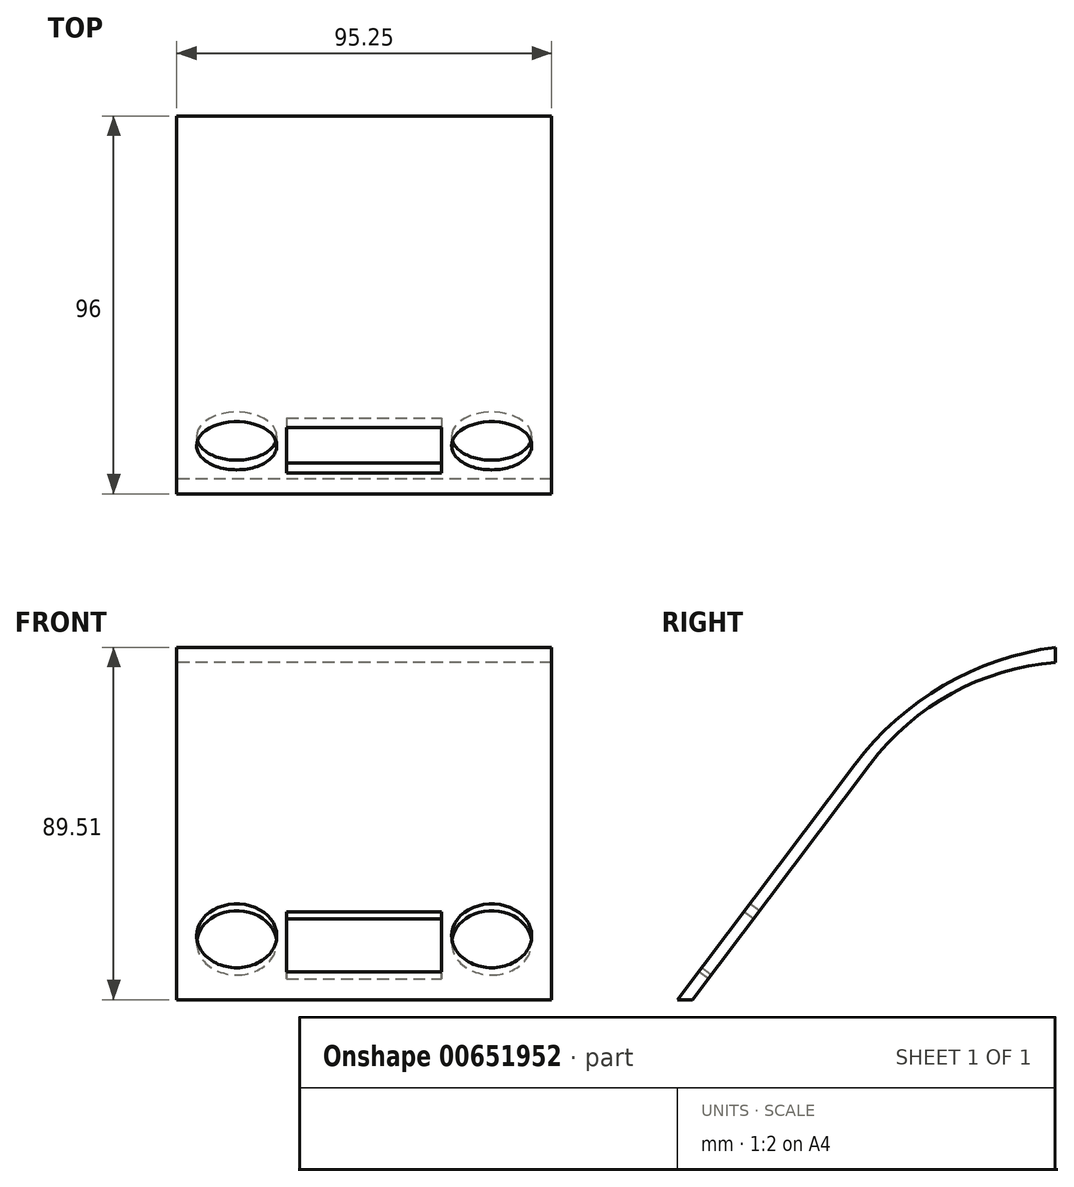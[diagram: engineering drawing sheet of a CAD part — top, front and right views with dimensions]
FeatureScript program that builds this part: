
annotation { "Feature Type Name" : "Feature", "Feature Type Description" : "" }
export const myFeature = defineFeature(function(context is Context, id is Id, definition is map)
    precondition{}
    {
        {
            var Q0;
            Q0=qCreatedBy(makeId("Right.planeOp"),FACE);
            var sketch = newSketch(context, id + "F0", { "sketchPlane" : qUnion([Q0])});
            skLineSegment(sketch, "E0", {"start": v(-8.65, 12.23) * mm, "end": v(-53.69, -47.57) * mm});
            skLineSegment(sketch, "E1", {"start": v(-53.69, -47.57) * mm, "end": v(-49.88, -47.57) * mm});
            skLineSegment(sketch, "E2", {"start": v(-49.88, -47.57) * mm, "end": v(-4.84, 12.23) * mm});
            skArc(sketch, "E3", {"start": v(42.31, 41.94) * mm, "mid": v(13.84, 32.22) * mm, "end": v(-8.65, 12.23) * mm});
            skArc(sketch, "E4", {"start": v(42.31, 38.13) * mm, "mid": v(15.96, 30.24) * mm, "end": v(-4.84, 12.23) * mm});
            skLineSegment(sketch, "E5", {"start": v(42.31, 41.94) * mm, "end": v(42.31, 38.13) * mm});
            skSolve(sketch);
        }
        {
            var Q0;
            Q0=makeQuery(id+"F0.imprint","IMPRINT",FACE,{"disambiguationData":[TD([[makeQuery(id+"F0.imprint","IMPRINT",EDGE,{"derivedFrom":sQuery(id+"F0.wireOp",EDGE,"E0")}),1.0]])]});
            extrude(context, id + "F1", {"entities" : qUnion([Q0]), "depth" : 95.25 * mm, "offsetDistance" : 25.4 * mm});
        }
        {
            var Q0;
            Q0=makeQuery(id+"F1.opExtrude","SWEPT_FACE",FACE,{"disambiguationData":[OSD([sQuery(id+"F0.wireOp",EDGE,"E0")])]});
            var sketch = newSketch(context, id + "F2", { "sketchPlane" : qUnion([Q0])});
            skCircle(sketch, "E6", {"center": v(15.24, -49.98) * mm, "radius": 10.16 * mm});
            skCircle(sketch, "E7", {"center": v(80.01, -49.98) * mm, "radius": 10.16 * mm});
            skLineSegment(sketch, "E8.bottom", {"start": v(27.94, -42.36) * mm, "end": v(67.31, -42.36) * mm});
            skLineSegment(sketch, "E8.top", {"start": v(27.94, -61.4) * mm, "end": v(67.31, -61.4) * mm});
            skLineSegment(sketch, "E8.left", {"start": v(27.94, -42.36) * mm, "end": v(27.94, -61.4) * mm});
            skLineSegment(sketch, "E8.right", {"start": v(67.31, -42.36) * mm, "end": v(67.31, -61.4) * mm});
            skSolve(sketch);
        }
        {
            var Q0;
            Q0=makeQuery(id+"F2.imprint","IMPRINT",FACE,{"disambiguationData":[TD([[makeQuery(id+"F2.imprint","IMPRINT",EDGE,{"derivedFrom":sQuery(id+"F2.wireOp",EDGE,"E6")}),1.0]])]});
            var Q1;
            Q1=makeQuery(id+"F2.imprint","IMPRINT",FACE,{"disambiguationData":[TD([[makeQuery(id+"F2.imprint","IMPRINT",EDGE,{"derivedFrom":sQuery(id+"F2.wireOp",EDGE,"E8.bottom")}),-1.0]])]});
            var Q2;
            Q2=makeQuery(id+"F2.imprint","IMPRINT",FACE,{"disambiguationData":[TD([[makeQuery(id+"F2.imprint","IMPRINT",EDGE,{"derivedFrom":sQuery(id+"F2.wireOp",EDGE,"E7")}),1.0]])]});
            extrude(context, id + "F3", {"entities" : qUnion([Q0, Q1, Q2]), "operationType" : NewBodyOperationType.REMOVE, "oppositeDirection" : true, "depth" : 25.4 * mm, "offsetDistance" : 25.4 * mm});
        }
    });
